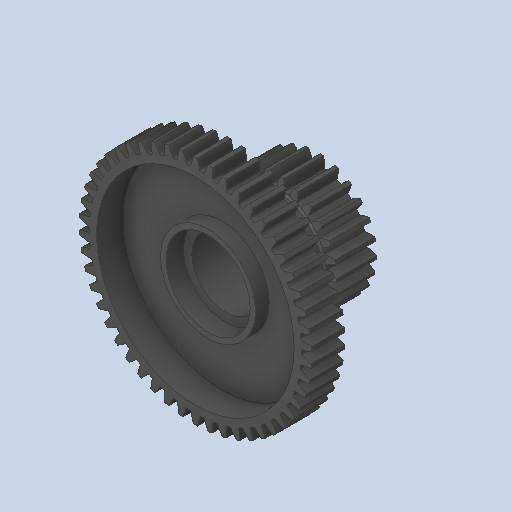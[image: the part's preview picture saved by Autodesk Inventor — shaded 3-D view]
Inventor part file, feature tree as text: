
AUTODESK INVENTOR PART (.ipt)
format: ipt  version: 2023 (Build 270158000, 158)  size: 570,368 bytes
history: native  units: in
note: dims shown in document units (in); Inventor stores cm internally (conversion verified against a paired STEP export)
features: chamfer x1
ambient origin geometry x8: Origin, YZ Plane, XZ Plane, XY Plane, X Axis, Y Axis, Z Axis, Center Point
bodies: Solid1 (feature_tree)
feature tree (1):
  chamfer  "Chamfer2"  [1 undecoded]
note: 1 required parameter value undecoded (feature->parameter linkage not recoverable at this tier; creation-order binding heuristic only, values carry confidence <= 0.55)
